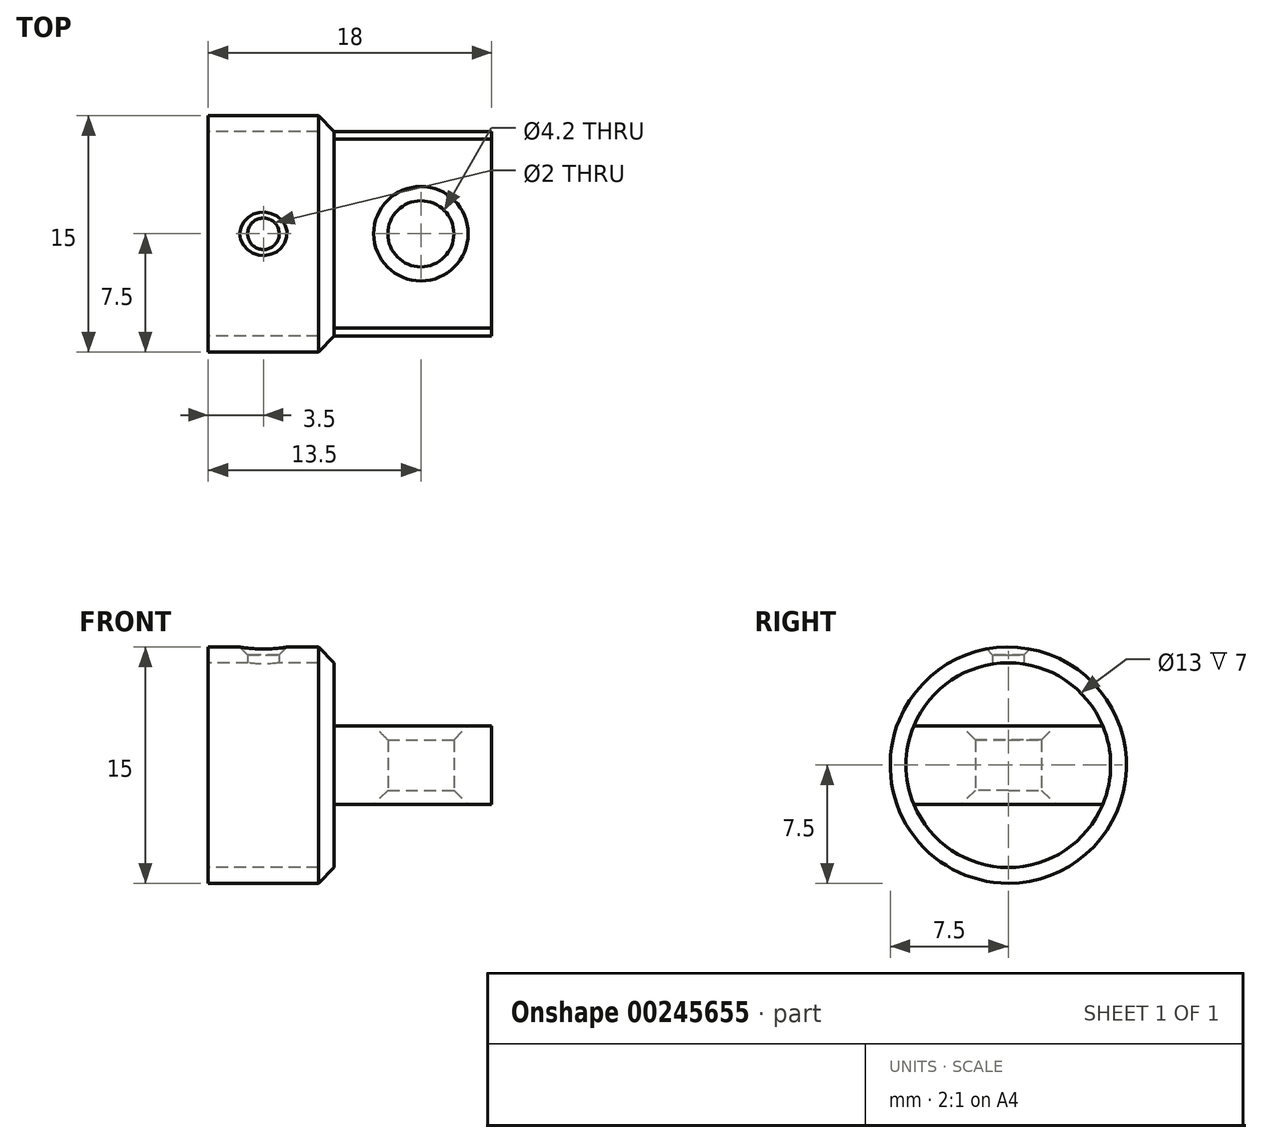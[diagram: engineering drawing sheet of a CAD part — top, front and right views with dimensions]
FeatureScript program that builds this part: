
annotation { "Feature Type Name" : "Feature", "Feature Type Description" : "" }
export const myFeature = defineFeature(function(context is Context, id is Id, definition is map)
    precondition{}
    {
        {
            var Q0;
            Q0=qCreatedBy(makeId("Right.planeOp"),FACE);
            var sketch = newSketch(context, id + "F0", { "sketchPlane" : qUnion([Q0])});
            skCircle(sketch, "E0", {"center": v(0, 0) * mm, "radius": 7.5 * mm});
            skSolve(sketch);
        }
        {
            var Q0;
            Q0 = qSketchRegion(id + "F0", true);
            extrude(context, id + "F1", {"entities" : qUnion([Q0]), "depth" : 8 * mm, "offsetDistance" : 25 * mm});
        }
        {
            var Q0;
            Q0=makeQuery(id+"F1.opExtrude","CAP_FACE",FACE,{"disambiguationData":[OSD([sQuery(id+"F0.wireOp",EDGE,"E0")])],"isStart":true});
            shell(context, id + "F2", {"entities" : qUnion([Q0]), "thickness" : 1 * mm});
        }
        {
            var Q0;
            Q0=makeQuery(id+"F1.opExtrude","CAP_EDGE",EDGE,{"disambiguationData":[OSD([sQuery(id+"F0.wireOp",EDGE,"E0")])],"isStart":false});
            chamfer(context, id + "F3", {"entities" : qUnion([Q0]), "width" : 1 * mm, "tangentPropagation" : true});
        }
        {
            var Q0;
            Q0=makeQuery(id+"F1.opExtrude","CAP_FACE",FACE,{"disambiguationData":[OSD([sQuery(id+"F0.wireOp",EDGE,"E0")])],"isStart":false});
            var sketch = newSketch(context, id + "F4", { "sketchPlane" : qUnion([Q0])});
            skLineSegment(sketch, "E1", {"start": v(0, -2.5) * mm, "end": v(-6, -2.5) * mm});
            skLineSegment(sketch, "E2", {"start": v(-6, -2.5) * mm, "end": v(6, -2.5) * mm});
            skLineSegment(sketch, "E3", {"start": v(0, 2.5) * mm, "end": v(6, 2.5) * mm});
            skLineSegment(sketch, "E4", {"start": v(0, 2.5) * mm, "end": v(-6, 2.5) * mm});
            skArc(sketch, "E5", {"start": v(-6, 2.5) * mm, "mid": v(-6.5, 0) * mm, "end": v(-6, -2.5) * mm});
            skArc(sketch, "E6", {"start": v(6, -2.5) * mm, "mid": v(6.5, 0) * mm, "end": v(6, 2.5) * mm});
            skSolve(sketch);
        }
        {
            var Q0;
            Q0 = qSketchRegion(id + "F4", true);
            extrude(context, id + "F5", {"entities" : qUnion([Q0]), "operationType" : NewBodyOperationType.ADD, "depth" : 10 * mm, "offsetDistance" : 25 * mm});
        }
        {
            var Q0;
            Q0=qCreatedBy(makeId("Top.planeOp"),FACE);
            cPlane(context, id + "F6", {"entities" : qUnion([Q0]), "cplaneType" : CPlaneType.OFFSET, "offset" : 2.5 * mm, "width" : 150 * mm, "height" : 150 * mm});
        }
        {
            var Q0;
            Q0=qCreatedBy(id+"F6.planeOp",FACE);
            var sketch = newSketch(context, id + "F7", { "sketchPlane" : qUnion([Q0])});
            skPoint(sketch, "E7", {"position": v(13.5, 0) * mm});
            skSolve(sketch);
        }
        {
            var Q0;
            Q0=sQuery(id+"F7.wireOp",VERTEX,"E7");
            var Q1;
            Q1=makeQuery(id+"F1.opExtrude","SWEPT_BODY",BODY,{"disambiguationData":[OSD([sQuery(id+"F0.wireOp",EDGE,"E0")])]});
            hole(context, id + "F8", {"style" : HoleStyle.C_SINK, "endStyle" : HoleEndStyle.BLIND, "holeDiameter" : 4.2 * mm, "cSinkDiameter" : 6 * mm, "cSinkAngle" : 90 * degree, "majorDiameter" : 5 * mm, "holeDepth" : 2.5 * mm, "isTappedThrough" : true, "tappedDepth" : 15 * mm, "tapClearance" : 0, "locations" : qUnion([Q0]), "scope" : qUnion([Q1]), "startStyle" : HoleStartStyle.SKETCH});
        }
        {
            var Q0;
            Q0=qCreatedBy(makeId("Top.planeOp"),FACE);
            cPlane(context, id + "F9", {"entities" : qUnion([Q0]), "cplaneType" : CPlaneType.OFFSET, "offset" : 2.5 * mm, "oppositeDirection" : true, "width" : 150 * mm, "height" : 150 * mm});
        }
        {
            var Q0;
            Q0=qCreatedBy(id+"F9.planeOp",FACE);
            var sketch = newSketch(context, id + "F10", { "sketchPlane" : qUnion([Q0])});
            skPoint(sketch, "E8", {"position": v(13.5, 0) * mm});
            skSolve(sketch);
        }
        {
            var Q0;
            Q0=sQuery(id+"F10.wireOp",VERTEX,"E8");
            var Q1;
            Q1=makeQuery(id+"F1.opExtrude","SWEPT_BODY",BODY,{"disambiguationData":[OSD([sQuery(id+"F0.wireOp",EDGE,"E0")])]});
            hole(context, id + "F11", {"style" : HoleStyle.C_SINK, "endStyle" : HoleEndStyle.BLIND, "oppositeDirection" : true, "holeDiameter" : 4.2 * mm, "cSinkDiameter" : 6 * mm, "cSinkAngle" : 90 * degree, "majorDiameter" : 5 * mm, "holeDepth" : 2.5 * mm, "isTappedThrough" : true, "tappedDepth" : 15 * mm, "tapClearance" : 0, "locations" : qUnion([Q0]), "scope" : qUnion([Q1]), "startStyle" : HoleStartStyle.SKETCH});
        }
        {
            var Q0;
            Q0=qCreatedBy(makeId("Right.planeOp"),FACE);
            var sketch = newSketch(context, id + "F12", { "sketchPlane" : qUnion([Q0])});
            skLineSegment(sketch, "E9", {"start": v(0, 0) * mm, "end": v(0, 7.5) * mm});
            skLineSegment(sketch, "E10.1.0", {"start": v(0, 0) * mm, "end": v(-6.5, -3.75) * mm});
            skLineSegment(sketch, "E10.2.0", {"start": v(0, 0) * mm, "end": v(6.5, -3.75) * mm});
            skPoint(sketch, "E10.center", {"position": v(0, 0) * mm});
            skSolve(sketch);
        }
        {
            var Q0;
            Q0=qCreatedBy(makeId("Top.planeOp"),FACE);
            cPlane(context, id + "F13", {"entities" : qUnion([Q0]), "cplaneType" : CPlaneType.OFFSET, "offset" : 7.5 * mm, "width" : 150 * mm, "height" : 150 * mm});
        }
        {
            var Q0;
            Q0=qCreatedBy(id+"F13.planeOp",FACE);
            var sketch = newSketch(context, id + "F14", { "sketchPlane" : qUnion([Q0])});
            skPoint(sketch, "E11", {"position": v(3.5, 0) * mm});
            skSolve(sketch);
        }
        {
            var Q0;
            Q0=sQuery(id+"F14.wireOp",VERTEX,"E11");
            var Q1;
            Q1=makeQuery(id+"F1.opExtrude","SWEPT_BODY",BODY,{"disambiguationData":[OSD([sQuery(id+"F0.wireOp",EDGE,"E0")])]});
            hole(context, id + "F15", {"style" : HoleStyle.C_SINK, "endStyle" : HoleEndStyle.BLIND, "holeDiameter" : 2 * mm, "cSinkDiameter" : 3 * mm, "cSinkAngle" : 90 * degree, "majorDiameter" : 5 * mm, "holeDepth" : 2.5 * mm, "isTappedThrough" : true, "tappedDepth" : 15 * mm, "tapClearance" : 0, "locations" : qUnion([Q0]), "scope" : qUnion([Q1]), "startStyle" : HoleStartStyle.SKETCH});
        }
    });
